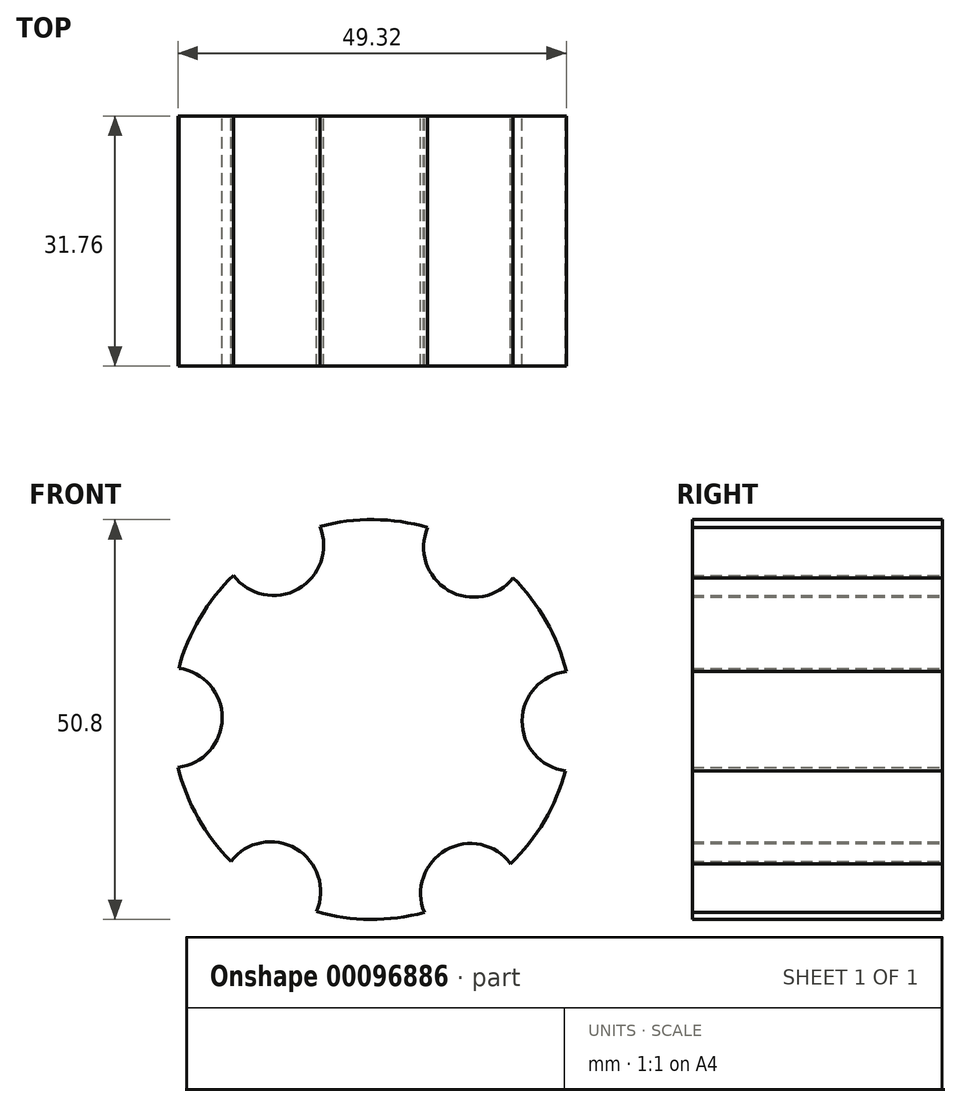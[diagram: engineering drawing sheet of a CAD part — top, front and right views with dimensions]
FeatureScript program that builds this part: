
annotation { "Feature Type Name" : "Feature", "Feature Type Description" : "" }
export const myFeature = defineFeature(function(context is Context, id is Id, definition is map)
    precondition{}
    {
        {
            var Q0;
            Q0=qCreatedBy(makeId("Front.planeOp"),FACE);
            var sketch = newSketch(context, id + "F0", { "sketchPlane" : qUnion([Q0])});
            skCircle(sketch, "E0.cCircle", {"center": v(0, 0) * mm, "radius": 25.4 * mm, "construction": true});
            skLineSegment(sketch, "E0.0", {"start": v(25.4, -0.22) * mm, "end": v(12.5, -22.1) * mm});
            skLineSegment(sketch, "E0.1", {"start": v(12.5, -22.1) * mm, "end": v(-12.9, -21.89) * mm});
            skLineSegment(sketch, "E0.2", {"start": v(-12.9, -21.89) * mm, "end": v(-25.4, 0.22) * mm});
            skLineSegment(sketch, "E0.3", {"start": v(-25.4, 0.22) * mm, "end": v(-12.5, 22.1) * mm});
            skLineSegment(sketch, "E0.4", {"start": v(-12.5, 22.1) * mm, "end": v(12.9, 21.89) * mm});
            skLineSegment(sketch, "E0.5", {"start": v(12.9, 21.89) * mm, "end": v(25.4, -0.22) * mm});
            skCircle(sketch, "E1", {"center": v(-25.4, 0.22) * mm, "radius": 6.35 * mm});
            skCircle(sketch, "E2", {"center": v(0, 0) * mm, "radius": 25.4 * mm});
            skCircle(sketch, "E3", {"center": v(-12.5, 22.1) * mm, "radius": 6.35 * mm});
            skCircle(sketch, "E4", {"center": v(12.9, 21.89) * mm, "radius": 6.35 * mm});
            skCircle(sketch, "E5", {"center": v(25.4, -0.22) * mm, "radius": 6.35 * mm});
            skCircle(sketch, "E6", {"center": v(12.5, -22.1) * mm, "radius": 6.35 * mm});
            skCircle(sketch, "E7", {"center": v(-12.9, -21.89) * mm, "radius": 6.35 * mm});
            skSolve(sketch);
        }
        {
            var Q0;
            {var subQ0=sQuery(id+"F0.wireOp",EDGE,"E5");var subQ1=sQuery(id+"F0.wireOp",EDGE,"E0.0");var subQ2=makeQuery(id+"F0.imprint","INTERSECT",VERTEX,{"derivedFrom":[subQ1,subQ0]});Q0=makeQuery(id+"F0.imprint","IMPRINT",FACE,{"disambiguationData":[TD([[makeQuery(id+"F0.imprint","IMPRINT",EDGE,{"disambiguationData":[TD([[subQ2,-1.0]])],"derivedFrom":subQ1}),1.0]])]});}
            var Q1;
            {var subQ0=sQuery(id+"F0.wireOp",EDGE,"E6");var subQ1=sQuery(id+"F0.wireOp",EDGE,"E0.1");var subQ2=makeQuery(id+"F0.imprint","INTERSECT",VERTEX,{"derivedFrom":[subQ1,subQ0]});Q1=makeQuery(id+"F0.imprint","IMPRINT",FACE,{"disambiguationData":[TD([[makeQuery(id+"F0.imprint","IMPRINT",EDGE,{"disambiguationData":[TD([[subQ2,-1.0]])],"derivedFrom":subQ1}),1.0]])]});}
            var Q2;
            {var subQ0=sQuery(id+"F0.wireOp",EDGE,"E7");var subQ1=sQuery(id+"F0.wireOp",EDGE,"E0.2");var subQ2=makeQuery(id+"F0.imprint","INTERSECT",VERTEX,{"derivedFrom":[subQ1,subQ0]});Q2=makeQuery(id+"F0.imprint","IMPRINT",FACE,{"disambiguationData":[TD([[makeQuery(id+"F0.imprint","IMPRINT",EDGE,{"disambiguationData":[TD([[subQ2,-1.0]])],"derivedFrom":subQ1}),1.0]])]});}
            var Q3;
            {var subQ0=sQuery(id+"F0.wireOp",EDGE,"E1");var subQ1=sQuery(id+"F0.wireOp",EDGE,"E0.3");var subQ2=makeQuery(id+"F0.imprint","INTERSECT",VERTEX,{"derivedFrom":[subQ1,subQ0]});Q3=makeQuery(id+"F0.imprint","IMPRINT",FACE,{"disambiguationData":[TD([[makeQuery(id+"F0.imprint","IMPRINT",EDGE,{"disambiguationData":[TD([[subQ2,-1.0]])],"derivedFrom":subQ1}),1.0]])]});}
            var Q4;
            {var subQ0=sQuery(id+"F0.wireOp",EDGE,"E3");var subQ1=sQuery(id+"F0.wireOp",EDGE,"E0.4");var subQ2=makeQuery(id+"F0.imprint","INTERSECT",VERTEX,{"derivedFrom":[subQ1,subQ0]});Q4=makeQuery(id+"F0.imprint","IMPRINT",FACE,{"disambiguationData":[TD([[makeQuery(id+"F0.imprint","IMPRINT",EDGE,{"disambiguationData":[TD([[subQ2,-1.0]])],"derivedFrom":subQ1}),1.0]])]});}
            var Q5;
            {var subQ0=sQuery(id+"F0.wireOp",EDGE,"E4");var subQ1=sQuery(id+"F0.wireOp",EDGE,"E0.5");var subQ2=makeQuery(id+"F0.imprint","INTERSECT",VERTEX,{"derivedFrom":[subQ1,subQ0]});Q5=makeQuery(id+"F0.imprint","IMPRINT",FACE,{"disambiguationData":[TD([[makeQuery(id+"F0.imprint","IMPRINT",EDGE,{"disambiguationData":[TD([[subQ2,-1.0]])],"derivedFrom":subQ1}),1.0]])]});}
            var Q6;
            {var subQ0=sQuery(id+"F0.wireOp",EDGE,"E5");var subQ1=sQuery(id+"F0.wireOp",EDGE,"E0.0");var subQ2=makeQuery(id+"F0.imprint","INTERSECT",VERTEX,{"derivedFrom":[subQ1,subQ0]});Q6=makeQuery(id+"F0.imprint","IMPRINT",FACE,{"disambiguationData":[TD([[makeQuery(id+"F0.imprint","IMPRINT",EDGE,{"disambiguationData":[TD([[subQ2,-1.0]])],"derivedFrom":subQ1}),-1.0]])]});}
            extrude(context, id + "F1", {"entities" : qUnion([Q0, Q1, Q2, Q3, Q4, Q5, Q6]), "endBound" : BoundingType.SYMMETRIC, "depth" : 31.75 * mm});
        }
    });
